# Revit family: LCOM-DFX
name_source: partatom
category: Lighting Fixtures
units: mm (PartAtom-declared; Revit-internal decimal feet)

## family parameters
Cut with Voids When Loaded = No
Host = Face
Light Source = Yes
OmniClass Number = 23.80.70.11.14.11
OmniClass Title = Downlights
Part Type = Normal
Room Calculation Point = No
Round Connector Dimension = Use Diameter
Shared = No

## types (8) — shared parameters
Color Filter = 16777215
Default Elevation = 4' - 0"
Description = Commercial-grade, LED strip luminaire
Dimming Lamp Color Temperature Shift = <None>
Housing Finish = Metal - Viscor - White
Lamp = LED
Lens Finish = Acrylic - Viscor - Frosted Round
Manufacturer = Visioneering By Viscor
Model = LCOM
Tilt Angle = -90.00°
URL = https://www.viscor.com
Voltage = 120 V
Width = 0' - 4 9/16"

## per-type parameters (varying)
| type | Apparent Load | Assembly Code | Emit from Line Length | Lamp Wattage | Length | Photometric Web File |
| LCOM-DFX48-LED840K032LUNV | 26 VA |  | 3' - 9 1/16" | 26 VA | 3' - 9 1/16" | LCOM-DFX48-LED840K032LUNV.ies |
| LCOM-DFX24-LED840K020LUNV | 16 VA | D5020200 | 1' - 11 1/8" | 16 VA | 1' - 11 1/8" | LCOM-DFX24-LED840K020LUNV.ies |
| LCOM-DFX24-LED840K032LUNV | 25 VA |  | 1' - 11 1/8" | 25 VA | 1' - 11 1/8" | LCOM-DFX24-LED840K032LUNV.ies |
| LCOM-DFX48-LED840K040LUNV | 33 VA |  | 3' - 9 1/16" | 33 VA | 3' - 9 1/16" | LCOM-DFX48-LED840K040LUNV.ies |
| LCOM-DFX48-LED840K050LUNV | 44 VA |  | 3' - 9 1/16" | 44 VA | 3' - 9 1/16" | LCOM-DFX48-LED840K050LUNV.ies |
| LCOM-DFX48-LED840K060LUNV | 54 VA |  | 3' - 9 1/16" | 54 VA | 3' - 9 1/16" | LCOM-DFX48-LED840K060LUNV.ies |
| LCOM-DFX48-UVA | 52 VA |  | 3' - 9 1/16" | 52 VA | 3' - 9 1/16" |  |
| LCOM-DFX24-UVA | 15 VA | D5020200 | 1' - 11 1/8" | 15 VA | 1' - 11 1/8" | LCOM-DFX24-UVA.ies |

## geometry (parser evidence)
native form markers: Sweep x3
no freeform markers — native parametric forms only
